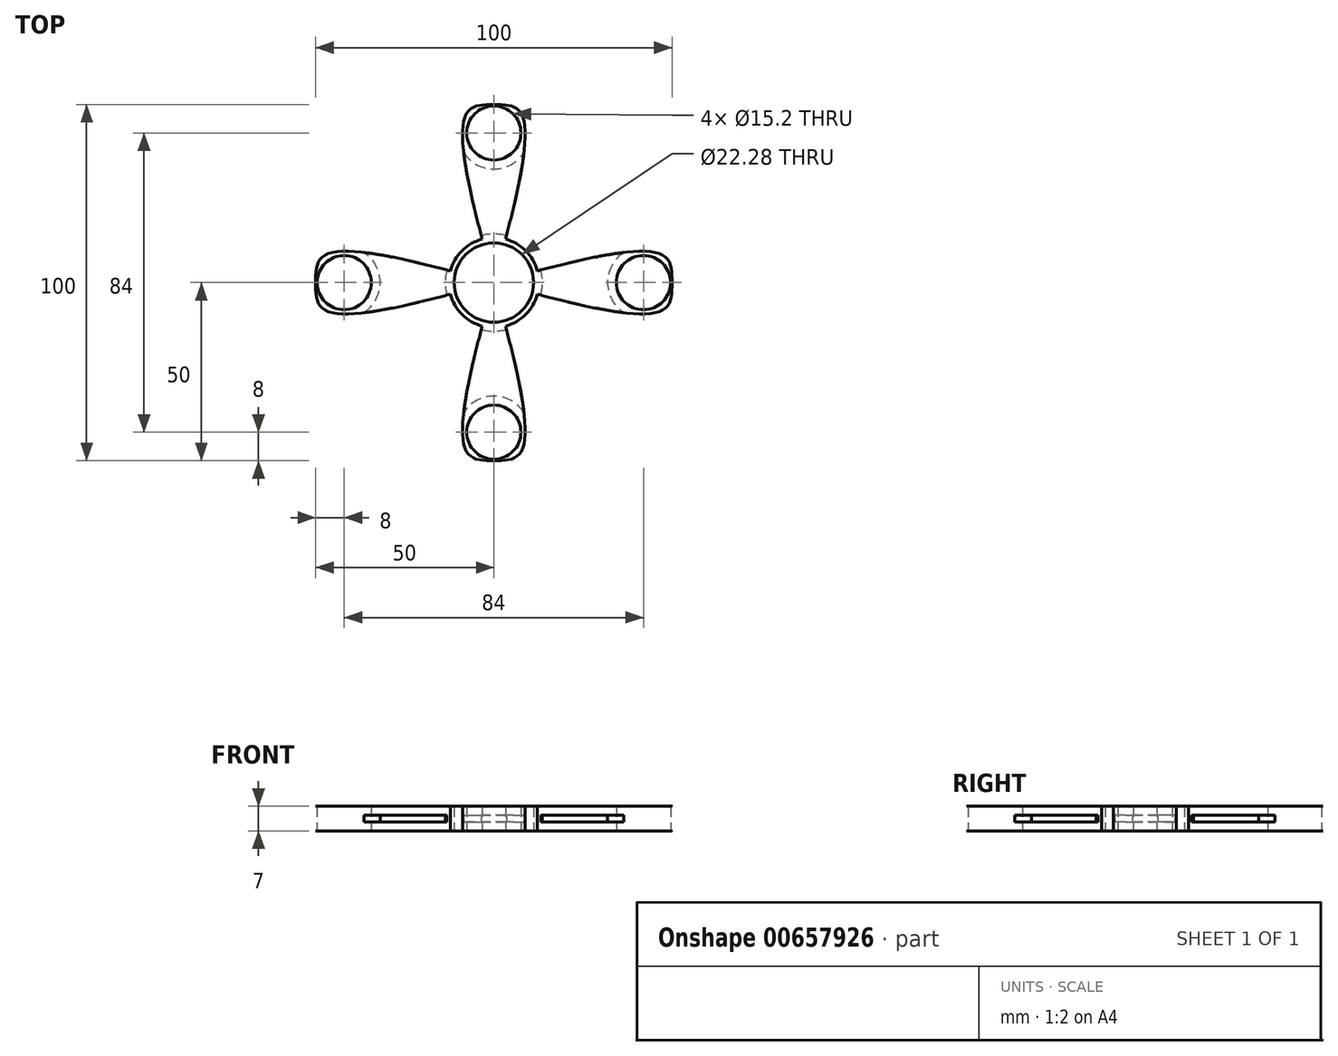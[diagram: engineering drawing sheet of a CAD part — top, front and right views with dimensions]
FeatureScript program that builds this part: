
annotation { "Feature Type Name" : "Feature", "Feature Type Description" : "" }
export const myFeature = defineFeature(function(context is Context, id is Id, definition is map)
    precondition{}
    {
        {
            var Q0;
            Q0=qCreatedBy(makeId("Top.planeOp"),FACE);
            var sketch = newSketch(context, id + "F0", { "sketchPlane" : qUnion([Q0])});
            skCircle(sketch, "E0", {"center": v(0, 0) * mm, "radius": 11.14 * mm});
            skCircle(sketch, "E1", {"center": v(0, 0) * mm, "radius": 12.64 * mm});
            skLineSegment(sketch, "E2", {"start": v(0, 0) * mm, "end": v(0, 50) * mm});
            skLineSegment(sketch, "E3.MirrorCS", {"start": v(0, 0) * mm, "end": v(0, -50) * mm});
            skLineSegment(sketch, "E4", {"start": v(0, 0) * mm, "end": v(50, 0) * mm});
            skLineSegment(sketch, "E5", {"start": v(0, 0) * mm, "end": v(-50, 0) * mm});
            skLineSegment(sketch, "E6", {"start": v(50, 0) * mm, "end": v(42, 0) * mm});
            skCircle(sketch, "E7", {"center": v(42, 0) * mm, "radius": 7.6 * mm});
            skCircle(sketch, "E8.MirrorC", {"center": v(-42, 0) * mm, "radius": 7.6 * mm});
            skFitSpline(sketch, "E9", {"points": [v(50, 0) * mm, v(47.55, 7.61) * mm, v(0, 0) * mm], "startDerivative": vector(0, 31.64) * mm, "endDerivative": vector(-87.7, -23.86) * mm});
            skFitSpline(sketch, "E10.MirrorCS", {"points": [v(-50, 0) * mm, v(-47.55, 7.61) * mm, v(0, 0) * mm], "startDerivative": vector(0, 31.64) * mm, "endDerivative": vector(87.7, -23.86) * mm});
            skFitSpline(sketch, "E11.MirrorCS", {"points": [v(50, 0) * mm, v(47.55, -7.61) * mm, v(0, 0) * mm], "startDerivative": vector(0, -31.64) * mm, "endDerivative": vector(-87.7, 23.86) * mm});
            skFitSpline(sketch, "E12.MirrorCS", {"points": [v(-50, 0) * mm, v(-47.55, -7.61) * mm, v(0, 0) * mm], "startDerivative": vector(0, -31.64) * mm, "endDerivative": vector(87.7, 23.86) * mm});
            skLineSegment(sketch, "E13", {"start": v(0, 50) * mm, "end": v(0, 42) * mm});
            skCircle(sketch, "E14", {"center": v(0, 42) * mm, "radius": 7.6 * mm});
            skLineSegment(sketch, "E15", {"start": v(0, 0) * mm, "end": v(8.94, 8.94) * mm});
            skFitSpline(sketch, "E16.MirrorCS", {"points": [v(0, 50) * mm, v(7.61, 47.55) * mm, v(0, 0) * mm], "startDerivative": vector(31.64, 0) * mm, "endDerivative": vector(-23.86, -87.7) * mm});
            skFitSpline(sketch, "E17.MirrorCS", {"points": [v(0, 50) * mm, v(-7.61, 47.55) * mm, v(0, 0) * mm], "startDerivative": vector(-31.64, 0) * mm, "endDerivative": vector(23.86, -87.7) * mm});
            skFitSpline(sketch, "E18.MirrorCS", {"points": [v(0, -50) * mm, v(-7.61, -47.55) * mm, v(0, 0) * mm], "startDerivative": vector(-31.64, 0) * mm, "endDerivative": vector(23.86, 87.7) * mm});
            skFitSpline(sketch, "E19.MirrorCS", {"points": [v(0, -50) * mm, v(7.61, -47.55) * mm, v(0, 0) * mm], "startDerivative": vector(31.64, 0) * mm, "endDerivative": vector(-23.86, 87.7) * mm});
            skCircle(sketch, "E20.MirrorC", {"center": v(0, -42) * mm, "radius": 7.6 * mm});
            skLineSegment(sketch, "E21", {"start": v(-5.65, 20.77) * mm, "end": v(5.65, 20.77) * mm});
            skLineSegment(sketch, "E22", {"start": v(20.77, 5.65) * mm, "end": v(20.77, -5.65) * mm});
            skLineSegment(sketch, "E23", {"start": v(-20.77, 5.65) * mm, "end": v(-20.77, -5.65) * mm});
            skLineSegment(sketch, "E24", {"start": v(-5.65, -20.77) * mm, "end": v(5.65, -20.77) * mm});
            skSolve(sketch);
        }
        {
            var Q0;
            {var subQ3=sQuery(id+"F0.wireOp",EDGE,"E22");var subQ6=sQuery(id+"F0.wireOp",EDGE,"E4");var subQ9=makeQuery(id+"F0.imprint","INTERSECT",VERTEX,{"derivedFrom":[subQ6,subQ3]});Q0=makeQuery(id+"F0.imprint","IMPRINT",FACE,{"disambiguationData":[TD([[makeQuery(id+"F0.imprint","IMPRINT",EDGE,{"disambiguationData":[TD([[subQ9,-1.0]])],"derivedFrom":subQ6}),-1.0]])]});}
            var Q1;
            {var subQ0=sQuery(id+"F0.wireOp",EDGE,"E17.MirrorCS");var subQ1=sQuery(id+"F0.wireOp",EDGE,"E0");var subQ2=makeQuery(id+"F0.imprint","INTERSECT",VERTEX,{"derivedFrom":[subQ1,subQ0]});Q1=makeQuery(id+"F0.imprint","IMPRINT",FACE,{"disambiguationData":[TD([[makeQuery(id+"F0.imprint","IMPRINT",EDGE,{"disambiguationData":[TD([[subQ2,-1.0]])],"derivedFrom":subQ1}),-1.0]])]});}
            var Q2;
            {var subQ0=sQuery(id+"F0.wireOp",EDGE,"E19.MirrorCS");var subQ1=sQuery(id+"F0.wireOp",EDGE,"E0");var subQ2=makeQuery(id+"F0.imprint","INTERSECT",VERTEX,{"derivedFrom":[subQ1,subQ0]});Q2=makeQuery(id+"F0.imprint","IMPRINT",FACE,{"disambiguationData":[TD([[makeQuery(id+"F0.imprint","IMPRINT",EDGE,{"disambiguationData":[TD([[subQ2,-1.0]])],"derivedFrom":subQ1}),-1.0]])]});}
            var Q3;
            {var subQ0=sQuery(id+"F0.wireOp",EDGE,"E16.MirrorCS");var subQ1=sQuery(id+"F0.wireOp",EDGE,"E1");var subQ2=makeQuery(id+"F0.imprint","INTERSECT",VERTEX,{"derivedFrom":[subQ1,subQ0]});Q3=makeQuery(id+"F0.imprint","IMPRINT",FACE,{"disambiguationData":[TD([[makeQuery(id+"F0.imprint","IMPRINT",EDGE,{"disambiguationData":[TD([[subQ2,-1.0]])],"derivedFrom":subQ1}),-1.0]])]});}
            var Q4;
            {var subQ0=sQuery(id+"F0.wireOp",EDGE,"E5");var subQ1=sQuery(id+"F0.wireOp",EDGE,"E0");var subQ2=makeQuery(id+"F0.imprint","INTERSECT",VERTEX,{"derivedFrom":[subQ1,subQ0]});Q4=makeQuery(id+"F0.imprint","IMPRINT",FACE,{"disambiguationData":[TD([[makeQuery(id+"F0.imprint","IMPRINT",EDGE,{"disambiguationData":[TD([[subQ2,-1.0]])],"derivedFrom":subQ1}),-1.0]])]});}
            var Q5;
            {var subQ0=sQuery(id+"F0.wireOp",EDGE,"E12.MirrorCS");var subQ1=sQuery(id+"F0.wireOp",EDGE,"E1");var subQ2=makeQuery(id+"F0.imprint","INTERSECT",VERTEX,{"derivedFrom":[subQ1,subQ0]});Q5=makeQuery(id+"F0.imprint","IMPRINT",FACE,{"disambiguationData":[TD([[makeQuery(id+"F0.imprint","IMPRINT",EDGE,{"disambiguationData":[TD([[subQ2,1.0]])],"derivedFrom":subQ1}),-1.0]])]});}
            var Q6;
            {var subQ0=sQuery(id+"F0.wireOp",EDGE,"E15");var subQ1=sQuery(id+"F0.wireOp",EDGE,"E0");var subQ2=makeQuery(id+"F0.imprint","INTERSECT",VERTEX,{"derivedFrom":[subQ1,subQ0]});Q6=makeQuery(id+"F0.imprint","IMPRINT",FACE,{"disambiguationData":[TD([[makeQuery(id+"F0.imprint","IMPRINT",EDGE,{"disambiguationData":[TD([[subQ2,-1.0]])],"derivedFrom":subQ1}),-1.0]])]});}
            var Q7;
            {var subQ3=sQuery(id+"F0.wireOp",EDGE,"E21");var subQ6=sQuery(id+"F0.wireOp",EDGE,"E2");var subQ9=makeQuery(id+"F0.imprint","INTERSECT",VERTEX,{"derivedFrom":[subQ6,subQ3]});Q7=makeQuery(id+"F0.imprint","IMPRINT",FACE,{"disambiguationData":[TD([[makeQuery(id+"F0.imprint","IMPRINT",EDGE,{"disambiguationData":[TD([[subQ9,-1.0]])],"derivedFrom":subQ6}),-1.0]])]});}
            var Q8;
            {var subQ0=sQuery(id+"F0.wireOp",EDGE,"E9");var subQ1=sQuery(id+"F0.wireOp",EDGE,"E0");var subQ2=makeQuery(id+"F0.imprint","INTERSECT",VERTEX,{"derivedFrom":[subQ1,subQ0]});Q8=makeQuery(id+"F0.imprint","IMPRINT",FACE,{"disambiguationData":[TD([[makeQuery(id+"F0.imprint","IMPRINT",EDGE,{"disambiguationData":[TD([[subQ2,-1.0]])],"derivedFrom":subQ1}),-1.0]])]});}
            var Q9;
            {var subQ0=sQuery(id+"F0.wireOp",EDGE,"E16.MirrorCS");var subQ1=sQuery(id+"F0.wireOp",EDGE,"E0");var subQ2=makeQuery(id+"F0.imprint","INTERSECT",VERTEX,{"derivedFrom":[subQ1,subQ0]});Q9=makeQuery(id+"F0.imprint","IMPRINT",FACE,{"disambiguationData":[TD([[makeQuery(id+"F0.imprint","IMPRINT",EDGE,{"disambiguationData":[TD([[subQ2,-1.0]])],"derivedFrom":subQ1}),-1.0]])]});}
            var Q10;
            {var subQ0=sQuery(id+"F0.wireOp",EDGE,"E17.MirrorCS");var subQ1=sQuery(id+"F0.wireOp",EDGE,"E1");var subQ2=makeQuery(id+"F0.imprint","INTERSECT",VERTEX,{"derivedFrom":[subQ1,subQ0]});Q10=makeQuery(id+"F0.imprint","IMPRINT",FACE,{"disambiguationData":[TD([[makeQuery(id+"F0.imprint","IMPRINT",EDGE,{"disambiguationData":[TD([[subQ2,1.0]])],"derivedFrom":subQ1}),-1.0]])]});}
            var Q11;
            {var subQ0=sQuery(id+"F0.wireOp",EDGE,"E2");var subQ1=sQuery(id+"F0.wireOp",EDGE,"E0");var subQ2=makeQuery(id+"F0.imprint","INTERSECT",VERTEX,{"derivedFrom":[subQ1,subQ0]});Q11=makeQuery(id+"F0.imprint","IMPRINT",FACE,{"disambiguationData":[TD([[makeQuery(id+"F0.imprint","IMPRINT",EDGE,{"disambiguationData":[TD([[subQ2,-1.0]])],"derivedFrom":subQ1}),-1.0]])]});}
            var Q12;
            {var subQ3=sQuery(id+"F0.wireOp",EDGE,"E22");var subQ7=sQuery(id+"F0.wireOp",EDGE,"E4");var subQ9=makeQuery(id+"F0.imprint","INTERSECT",VERTEX,{"derivedFrom":[subQ7,subQ3]});Q12=makeQuery(id+"F0.imprint","IMPRINT",FACE,{"disambiguationData":[TD([[makeQuery(id+"F0.imprint","IMPRINT",EDGE,{"disambiguationData":[TD([[subQ9,-1.0]])],"derivedFrom":subQ7}),1.0]])]});}
            var Q13;
            {var subQ0=sQuery(id+"F0.wireOp",EDGE,"E11.MirrorCS");var subQ1=sQuery(id+"F0.wireOp",EDGE,"E1");var subQ2=makeQuery(id+"F0.imprint","INTERSECT",VERTEX,{"derivedFrom":[subQ1,subQ0]});Q13=makeQuery(id+"F0.imprint","IMPRINT",FACE,{"disambiguationData":[TD([[makeQuery(id+"F0.imprint","IMPRINT",EDGE,{"disambiguationData":[TD([[subQ2,-1.0]])],"derivedFrom":subQ1}),-1.0]])]});}
            var Q14;
            {var subQ0=sQuery(id+"F0.wireOp",EDGE,"E10.MirrorCS");var subQ1=sQuery(id+"F0.wireOp",EDGE,"E1");var subQ2=makeQuery(id+"F0.imprint","INTERSECT",VERTEX,{"derivedFrom":[subQ1,subQ0]});Q14=makeQuery(id+"F0.imprint","IMPRINT",FACE,{"disambiguationData":[TD([[makeQuery(id+"F0.imprint","IMPRINT",EDGE,{"disambiguationData":[TD([[subQ2,-1.0]])],"derivedFrom":subQ1}),-1.0]])]});}
            var Q15;
            {var subQ0=sQuery(id+"F0.wireOp",EDGE,"E4");var subQ1=sQuery(id+"F0.wireOp",EDGE,"E0");var subQ2=makeQuery(id+"F0.imprint","INTERSECT",VERTEX,{"derivedFrom":[subQ1,subQ0]});Q15=makeQuery(id+"F0.imprint","IMPRINT",FACE,{"disambiguationData":[TD([[makeQuery(id+"F0.imprint","IMPRINT",EDGE,{"disambiguationData":[TD([[subQ2,1.0]])],"derivedFrom":subQ1}),-1.0]])]});}
            var Q16;
            {var subQ1=sQuery(id+"F0.wireOp",EDGE,"E2");var subQ5=sQuery(id+"F0.wireOp",EDGE,"E21");var subQ8=makeQuery(id+"F0.imprint","INTERSECT",VERTEX,{"derivedFrom":[subQ1,subQ5]});Q16=makeQuery(id+"F0.imprint","IMPRINT",FACE,{"disambiguationData":[TD([[makeQuery(id+"F0.imprint","IMPRINT",EDGE,{"disambiguationData":[TD([[subQ8,-1.0]])],"derivedFrom":subQ1}),1.0]])]});}
            var Q17;
            {var subQ1=sQuery(id+"F0.wireOp",EDGE,"E5");var subQ3=sQuery(id+"F0.wireOp",EDGE,"E23");var subQ8=makeQuery(id+"F0.imprint","INTERSECT",VERTEX,{"derivedFrom":[subQ1,subQ3]});Q17=makeQuery(id+"F0.imprint","IMPRINT",FACE,{"disambiguationData":[TD([[makeQuery(id+"F0.imprint","IMPRINT",EDGE,{"disambiguationData":[TD([[subQ8,-1.0]])],"derivedFrom":subQ1}),-1.0]])]});}
            var Q18;
            {var subQ0=sQuery(id+"F0.wireOp",EDGE,"E10.MirrorCS");var subQ1=sQuery(id+"F0.wireOp",EDGE,"E0");var subQ2=makeQuery(id+"F0.imprint","INTERSECT",VERTEX,{"derivedFrom":[subQ1,subQ0]});Q18=makeQuery(id+"F0.imprint","IMPRINT",FACE,{"disambiguationData":[TD([[makeQuery(id+"F0.imprint","IMPRINT",EDGE,{"disambiguationData":[TD([[subQ2,-1.0]])],"derivedFrom":subQ1}),-1.0]])]});}
            var Q19;
            {var subQ0=sQuery(id+"F0.wireOp",EDGE,"E3.MirrorCS");var subQ1=sQuery(id+"F0.wireOp",EDGE,"E0");var subQ2=makeQuery(id+"F0.imprint","INTERSECT",VERTEX,{"derivedFrom":[subQ1,subQ0]});Q19=makeQuery(id+"F0.imprint","IMPRINT",FACE,{"disambiguationData":[TD([[makeQuery(id+"F0.imprint","IMPRINT",EDGE,{"disambiguationData":[TD([[subQ2,-1.0]])],"derivedFrom":subQ1}),-1.0]])]});}
            var Q20;
            {var subQ0=sQuery(id+"F0.wireOp",EDGE,"E19.MirrorCS");var subQ1=sQuery(id+"F0.wireOp",EDGE,"E1");var subQ2=makeQuery(id+"F0.imprint","INTERSECT",VERTEX,{"derivedFrom":[subQ1,subQ0]});Q20=makeQuery(id+"F0.imprint","IMPRINT",FACE,{"disambiguationData":[TD([[makeQuery(id+"F0.imprint","IMPRINT",EDGE,{"disambiguationData":[TD([[subQ2,1.0]])],"derivedFrom":subQ1}),-1.0]])]});}
            var Q21;
            {var subQ0=sQuery(id+"F0.wireOp",EDGE,"E9");var subQ1=sQuery(id+"F0.wireOp",EDGE,"E1");var subQ2=makeQuery(id+"F0.imprint","INTERSECT",VERTEX,{"derivedFrom":[subQ1,subQ0]});Q21=makeQuery(id+"F0.imprint","IMPRINT",FACE,{"disambiguationData":[TD([[makeQuery(id+"F0.imprint","IMPRINT",EDGE,{"disambiguationData":[TD([[subQ2,1.0]])],"derivedFrom":subQ1}),-1.0]])]});}
            var Q22;
            {var subQ0=sQuery(id+"F0.wireOp",EDGE,"E9");var subQ1=sQuery(id+"F0.wireOp",EDGE,"E0");var subQ2=makeQuery(id+"F0.imprint","INTERSECT",VERTEX,{"derivedFrom":[subQ1,subQ0]});Q22=makeQuery(id+"F0.imprint","IMPRINT",FACE,{"disambiguationData":[TD([[makeQuery(id+"F0.imprint","IMPRINT",EDGE,{"disambiguationData":[TD([[subQ2,1.0]])],"derivedFrom":subQ1}),-1.0]])]});}
            var Q23;
            {var subQ0=sQuery(id+"F0.wireOp",EDGE,"E18.MirrorCS");var subQ1=sQuery(id+"F0.wireOp",EDGE,"E1");var subQ2=makeQuery(id+"F0.imprint","INTERSECT",VERTEX,{"derivedFrom":[subQ1,subQ0]});Q23=makeQuery(id+"F0.imprint","IMPRINT",FACE,{"disambiguationData":[TD([[makeQuery(id+"F0.imprint","IMPRINT",EDGE,{"disambiguationData":[TD([[subQ2,-1.0]])],"derivedFrom":subQ1}),-1.0]])]});}
            var Q24;
            {var subQ1=sQuery(id+"F0.wireOp",EDGE,"E5");var subQ3=sQuery(id+"F0.wireOp",EDGE,"E23");var subQ5=makeQuery(id+"F0.imprint","INTERSECT",VERTEX,{"derivedFrom":[subQ1,subQ3]});Q24=makeQuery(id+"F0.imprint","IMPRINT",FACE,{"disambiguationData":[TD([[makeQuery(id+"F0.imprint","IMPRINT",EDGE,{"disambiguationData":[TD([[subQ5,-1.0]])],"derivedFrom":subQ1}),1.0]])]});}
            var Q25;
            {var subQ0=sQuery(id+"F0.wireOp",EDGE,"E12.MirrorCS");var subQ1=sQuery(id+"F0.wireOp",EDGE,"E0");var subQ2=makeQuery(id+"F0.imprint","INTERSECT",VERTEX,{"derivedFrom":[subQ1,subQ0]});Q25=makeQuery(id+"F0.imprint","IMPRINT",FACE,{"disambiguationData":[TD([[makeQuery(id+"F0.imprint","IMPRINT",EDGE,{"disambiguationData":[TD([[subQ2,-1.0]])],"derivedFrom":subQ1}),-1.0]])]});}
            var Q26;
            {var subQ0=sQuery(id+"F0.wireOp",EDGE,"E18.MirrorCS");var subQ1=sQuery(id+"F0.wireOp",EDGE,"E0");var subQ2=makeQuery(id+"F0.imprint","INTERSECT",VERTEX,{"derivedFrom":[subQ1,subQ0]});Q26=makeQuery(id+"F0.imprint","IMPRINT",FACE,{"disambiguationData":[TD([[makeQuery(id+"F0.imprint","IMPRINT",EDGE,{"disambiguationData":[TD([[subQ2,-1.0]])],"derivedFrom":subQ1}),-1.0]])]});}
            var Q27;
            {var subQ1=sQuery(id+"F0.wireOp",EDGE,"E3.MirrorCS");var subQ6=sQuery(id+"F0.wireOp",EDGE,"E24");var subQ8=makeQuery(id+"F0.imprint","INTERSECT",VERTEX,{"derivedFrom":[subQ1,subQ6]});Q27=makeQuery(id+"F0.imprint","IMPRINT",FACE,{"disambiguationData":[TD([[makeQuery(id+"F0.imprint","IMPRINT",EDGE,{"disambiguationData":[TD([[subQ8,-1.0]])],"derivedFrom":subQ1}),-1.0]])]});}
            var Q28;
            {var subQ1=sQuery(id+"F0.wireOp",EDGE,"E3.MirrorCS");var subQ6=sQuery(id+"F0.wireOp",EDGE,"E24");var subQ8=makeQuery(id+"F0.imprint","INTERSECT",VERTEX,{"derivedFrom":[subQ1,subQ6]});Q28=makeQuery(id+"F0.imprint","IMPRINT",FACE,{"disambiguationData":[TD([[makeQuery(id+"F0.imprint","IMPRINT",EDGE,{"disambiguationData":[TD([[subQ8,-1.0]])],"derivedFrom":subQ1}),1.0]])]});}
            extrude(context, id + "F1", {"entities" : qUnion([Q0, Q1, Q2, Q3, Q4, Q5, Q6, Q7, Q8, Q9, Q10, Q11, Q12, Q13, Q14, Q15, Q16, Q17, Q18, Q19, Q20, Q21, Q22, Q23, Q24, Q25, Q26, Q27, Q28]), "depth" : 7 * mm, "offsetDistance" : 25 * mm});
        }
        {
            var Q0;
            Q0=makeQuery(id+"F1.opExtrude","SWEPT_FACE",FACE,{"disambiguationData":[OSD([sQuery(id+"F0.wireOp",EDGE,"E10.MirrorCS")])]});
            var Q1;
            Q1=makeQuery(id+"F1.opExtrude","SWEPT_FACE",FACE,{"disambiguationData":[OSD([sQuery(id+"F0.wireOp",EDGE,"E12.MirrorCS")])]});
            var Q2;
            Q2=makeQuery(id+"F1.opExtrude","SWEPT_FACE",FACE,{"disambiguationData":[OSD([sQuery(id+"F0.wireOp",EDGE,"E19.MirrorCS")])]});
            var Q3;
            Q3=makeQuery(id+"F1.opExtrude","SWEPT_FACE",FACE,{"disambiguationData":[OSD([sQuery(id+"F0.wireOp",EDGE,"E18.MirrorCS")])]});
            var Q4;
            Q4=makeQuery(id+"F1.opExtrude","SWEPT_FACE",FACE,{"disambiguationData":[OSD([sQuery(id+"F0.wireOp",EDGE,"E11.MirrorCS")])]});
            var Q5;
            Q5=makeQuery(id+"F1.opExtrude","SWEPT_FACE",FACE,{"disambiguationData":[OSD([sQuery(id+"F0.wireOp",EDGE,"E9")])]});
            var Q6;
            Q6=makeQuery(id+"F1.opExtrude","SWEPT_FACE",FACE,{"disambiguationData":[OSD([sQuery(id+"F0.wireOp",EDGE,"E16.MirrorCS")])]});
            var Q7;
            Q7=makeQuery(id+"F1.opExtrude","SWEPT_FACE",FACE,{"disambiguationData":[OSD([sQuery(id+"F0.wireOp",EDGE,"E17.MirrorCS")])]});
            shell(context, id + "F2", {"entities" : qUnion([Q0, Q1, Q2, Q3, Q4, Q5, Q6, Q7]), "thickness" : 2.5 * mm});
        }
    });
